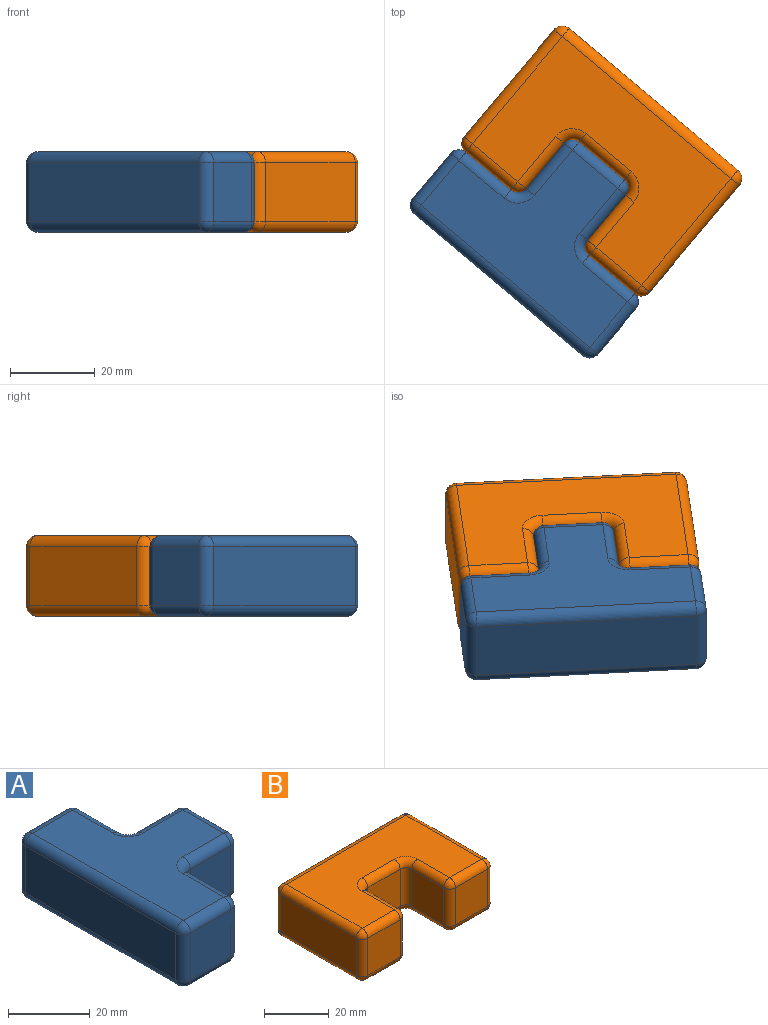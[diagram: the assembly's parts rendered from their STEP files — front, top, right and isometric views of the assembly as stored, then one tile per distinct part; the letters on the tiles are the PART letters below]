
ASSEMBLY  parts=2 mates=1
PART A: 50 faces, bbox 38.1x57.2x19.1 mm
  f0: plane 52.07x33.02mm, normal (0,0,-1), area 1004.6mm2, adj f18,f19,f24,f25,f29,f35,f40,f43
  f1: plane 14.04x13.97mm, normal (1,0,0), area 196.1mm2, adj f12,f13,f19,f20
  f2: plane 52.07x13.97mm, normal (-1,0,0), area 727.4mm2, adj f14,f23,f24,f48
  f3: plane 13.97x13.9mm, normal (1,0,0), area 194.2mm2, adj f33,f34,f42,f43
  f4: plane 52.07x33.02mm, normal (0,0,1), area 1004.6mm2, adj f11,f13,f14,f16,f21,f22,f31,f32
  f5: plane 13.97x13.97mm, normal (0,-1,0), area 195.2mm2, adj f11,f12,f18,f48
  f6: plane 13.97x13.97mm, normal (0,1,0), area 195.2mm2, adj f22,f23,f34,f35
  f7: plane 13.97x13.97mm, normal (0,-1,0), area 195.2mm2, adj f20,f21,f29,f30
  f8: plane 13.97x13.97mm, normal (0,1,0), area 195.2mm2, adj f32,f41,f42,f46
  f9: plane 13.97x13.97mm, normal (1,0,0), area 195.2mm2, adj f30,f31,f40,f41
  f10: sphere r=2.54mm, area 10.1mm2, adj f11,f12,f13
  f11: cylinder r=2.54mm len=13.97mm, axis (1,0,0), area 55.7mm2, adj f4,f5,f10,f47
  f12: cylinder r=2.54mm len=13.97mm, axis (0,0,-1), area 55.7mm2, adj f1,f5,f10,f15
  f13: cylinder r=2.54mm len=14.04mm, axis (0,-1,0), area 56mm2, adj f1,f4,f10,f16
  f14: cylinder r=2.54mm len=52.07mm, axis (0,1,0), area 207.8mm2, adj f2,f4,f17,f47
  f15: sphere r=2.54mm, area 10.1mm2, adj f12,f18,f19
  f16: torus R=5.08mm, axis (0,0,1), area 21.7mm2, adj f4,f13,f20,f21
  f17: sphere r=2.54mm, area 10.1mm2, adj f14,f22,f23
  f18: cylinder r=2.54mm len=13.97mm, axis (-1,0,0), area 55.7mm2, adj f0,f5,f15,f49
  f19: cylinder r=2.54mm len=14.04mm, axis (0,1,0), area 56mm2, adj f0,f1,f15,f25
  f20: cylinder r=2.54mm len=13.97mm, axis (0,0,1), area 55.7mm2, adj f1,f7,f16,f25
  f21: cylinder r=2.54mm len=13.97mm, axis (1,0,0), area 55.7mm2, adj f4,f7,f16,f26
  f22: cylinder r=2.54mm len=13.97mm, axis (-1,0,0), area 55.7mm2, adj f4,f6,f17,f27
  f23: cylinder r=2.54mm len=13.97mm, axis (0,0,-1), area 55.7mm2, adj f2,f6,f17,f28
  f24: cylinder r=2.54mm len=52.07mm, axis (0,-1,0), area 207.8mm2, adj f0,f2,f28,f49
  f25: torus R=5.08mm, axis (0,0,1), area 21.7mm2, adj f0,f19,f20,f29
  f26: sphere r=2.54mm, area 10.1mm2, adj f21,f30,f31
  f27: sphere r=2.54mm, area 10.1mm2, adj f22,f33,f34
  f28: sphere r=2.54mm, area 10.1mm2, adj f23,f24,f35
  f29: cylinder r=2.54mm len=13.97mm, axis (-1,0,0), area 55.7mm2, adj f0,f7,f25,f36
  f30: cylinder r=2.54mm len=13.97mm, axis (0,0,1), area 55.7mm2, adj f7,f9,f26,f36
  f31: cylinder r=2.54mm len=13.97mm, axis (0,1,0), area 55.7mm2, adj f4,f9,f26,f37
  f32: cylinder r=2.54mm len=13.97mm, axis (-1,0,0), area 55.7mm2, adj f4,f8,f37,f38
  f33: cylinder r=2.54mm len=13.9mm, axis (0,-1,0), area 55.5mm2, adj f3,f4,f27,f38
  f34: cylinder r=2.54mm len=13.97mm, axis (0,0,1), area 55.7mm2, adj f3,f6,f27,f39
  f35: cylinder r=2.54mm len=13.97mm, axis (1,0,0), area 55.7mm2, adj f0,f6,f28,f39
  f36: sphere r=2.54mm, area 10.1mm2, adj f29,f30,f40
  f37: sphere r=2.54mm, area 10.1mm2, adj f31,f32,f41
  f38: torus R=5.08mm, axis (0,0,1), area 21.7mm2, adj f4,f32,f33,f42
  f39: sphere r=2.54mm, area 10.1mm2, adj f34,f35,f43
  f40: cylinder r=2.54mm len=13.97mm, axis (0,-1,0), area 55.7mm2, adj f0,f9,f36,f44
  f41: cylinder r=2.54mm len=13.97mm, axis (0,0,-1), area 55.7mm2, adj f8,f9,f37,f44
  f42: cylinder r=2.54mm len=13.97mm, axis (0,0,-1), area 55.7mm2, adj f3,f8,f38,f45
  f43: cylinder r=2.54mm len=13.9mm, axis (0,1,0), area 55.5mm2, adj f0,f3,f39,f45
  f44: sphere r=2.54mm, area 10.1mm2, adj f40,f41,f46
  f45: torus R=5.08mm, axis (0,0,1), area 21.7mm2, adj f0,f42,f43,f46
  f46: cylinder r=2.54mm len=13.97mm, axis (1,0,0), area 55.7mm2, adj f0,f8,f44,f45
  f47: sphere r=2.54mm, area 10.1mm2, adj f11,f14,f48
  f48: cylinder r=2.54mm len=13.97mm, axis (0,0,1), area 55.7mm2, adj f2,f5,f47,f49
  f49: sphere r=2.54mm, area 10.1mm2, adj f18,f24,f48
PART B: 50 faces, bbox 57.2x38.1x19.1 mm
  f0: plane 33.02x13.97mm, normal (-1,0,0), area 461.3mm2, adj f10,f13,f16,f17
  f1: plane 52.07x33.02mm, normal (0,0,-1), area 1270.8mm2, adj f10,f14,f15,f24,f25,f30,f34,f35
  f2: plane 33.02x13.97mm, normal (1,0,0), area 461.3mm2, adj f23,f24,f32,f33
  f3: plane 52.07x33.02mm, normal (0,0,1), area 1270.8mm2, adj f17,f22,f27,f32,f38,f42,f43,f46
  f4: plane 13.97x13.97mm, normal (0,-1,0), area 195.2mm2, adj f36,f37,f45,f46
  f5: plane 52.07x13.97mm, normal (0,1,0), area 727.4mm2, adj f13,f14,f22,f23
  f6: plane 13.97x13.97mm, normal (1,0,0), area 195.2mm2, adj f25,f26,f37,f38
  f7: plane 13.97x13.97mm, normal (0,-1,0), area 195.2mm2, adj f15,f16,f26,f27
  f8: plane 13.97x13.97mm, normal (-1,0,0), area 195.2mm2, adj f35,f44,f45,f49
  f9: plane 13.97x13.97mm, normal (0,-1,0), area 195.2mm2, adj f33,f34,f43,f44
  f10: cylinder r=2.54mm len=33.02mm, axis (0,-1,0), area 131.7mm2, adj f0,f1,f11,f12
  f11: sphere r=2.54mm, area 10.1mm2, adj f10,f13,f14
  f12: sphere r=2.54mm, area 10.1mm2, adj f10,f15,f16
  f13: cylinder r=2.54mm len=13.97mm, axis (0,0,-1), area 55.7mm2, adj f0,f5,f11,f18
  f14: cylinder r=2.54mm len=52.07mm, axis (1,0,0), area 207.8mm2, adj f1,f5,f11,f19
  f15: cylinder r=2.54mm len=13.97mm, axis (-1,0,0), area 55.7mm2, adj f1,f7,f12,f20
  f16: cylinder r=2.54mm len=13.97mm, axis (0,0,1), area 55.7mm2, adj f0,f7,f12,f21
  f17: cylinder r=2.54mm len=33.02mm, axis (0,1,0), area 131.7mm2, adj f0,f3,f18,f21
  f18: sphere r=2.54mm, area 10.1mm2, adj f13,f17,f22
  f19: sphere r=2.54mm, area 10.1mm2, adj f14,f23,f24
  f20: sphere r=2.54mm, area 10.1mm2, adj f15,f25,f26
  f21: sphere r=2.54mm, area 10.1mm2, adj f16,f17,f27
  f22: cylinder r=2.54mm len=52.07mm, axis (-1,0,0), area 207.8mm2, adj f3,f5,f18,f28
  f23: cylinder r=2.54mm len=13.97mm, axis (0,0,1), area 55.7mm2, adj f2,f5,f19,f28
  f24: cylinder r=2.54mm len=33.02mm, axis (0,1,0), area 131.7mm2, adj f1,f2,f19,f29
  f25: cylinder r=2.54mm len=13.97mm, axis (0,1,0), area 55.7mm2, adj f1,f6,f20,f30
  f26: cylinder r=2.54mm len=13.97mm, axis (0,0,-1), area 55.7mm2, adj f6,f7,f20,f31
  f27: cylinder r=2.54mm len=13.97mm, axis (1,0,0), area 55.7mm2, adj f3,f7,f21,f31
  f28: sphere r=2.54mm, area 10.1mm2, adj f22,f23,f32
  f29: sphere r=2.54mm, area 10.1mm2, adj f24,f33,f34
  f30: torus R=5.08mm, axis (0,0,1), area 21.7mm2, adj f1,f25,f36,f37
  f31: sphere r=2.54mm, area 10.1mm2, adj f26,f27,f38
  f32: cylinder r=2.54mm len=33.02mm, axis (0,-1,0), area 131.7mm2, adj f2,f3,f28,f39
  f33: cylinder r=2.54mm len=13.97mm, axis (0,0,-1), area 55.7mm2, adj f2,f9,f29,f39
  f34: cylinder r=2.54mm len=13.97mm, axis (-1,0,0), area 55.7mm2, adj f1,f9,f29,f40
  f35: cylinder r=2.54mm len=13.97mm, axis (0,1,0), area 55.7mm2, adj f1,f8,f40,f41
  f36: cylinder r=2.54mm len=13.97mm, axis (-1,0,0), area 55.7mm2, adj f1,f4,f30,f41
  f37: cylinder r=2.54mm len=13.97mm, axis (0,0,1), area 55.7mm2, adj f4,f6,f30,f42
  f38: cylinder r=2.54mm len=13.97mm, axis (0,-1,0), area 55.7mm2, adj f3,f6,f31,f42
  f39: sphere r=2.54mm, area 10.1mm2, adj f32,f33,f43
  f40: sphere r=2.54mm, area 10.1mm2, adj f34,f35,f44
  f41: torus R=5.08mm, axis (0,0,1), area 21.7mm2, adj f1,f35,f36,f45
  f42: torus R=5.08mm, axis (0,0,1), area 21.7mm2, adj f3,f37,f38,f46
  f43: cylinder r=2.54mm len=13.97mm, axis (1,0,0), area 55.7mm2, adj f3,f9,f39,f47
  f44: cylinder r=2.54mm len=13.97mm, axis (0,0,1), area 55.7mm2, adj f8,f9,f40,f47
  f45: cylinder r=2.54mm len=13.97mm, axis (0,0,-1), area 55.7mm2, adj f4,f8,f41,f48
  f46: cylinder r=2.54mm len=13.97mm, axis (1,0,0), area 55.7mm2, adj f3,f4,f42,f48
  f47: sphere r=2.54mm, area 10.1mm2, adj f43,f44,f49
  f48: torus R=5.08mm, axis (0,0,1), area 21.7mm2, adj f3,f45,f46,f49
  f49: cylinder r=2.54mm len=13.97mm, axis (0,-1,0), area 55.7mm2, adj f3,f8,f47,f48
PLACE A rot(axis=(0,0,1),50deg) t=(-6.01,13,-22.25)mm
PLACE B rot(axis=(0,0,-1),40deg) t=(30.68,56.83,-22.25)mm
MATE parallel A.f9 <-> B.f4  axis (0.64,0.77,0) through (40.32,23.86,-12.72)mm
